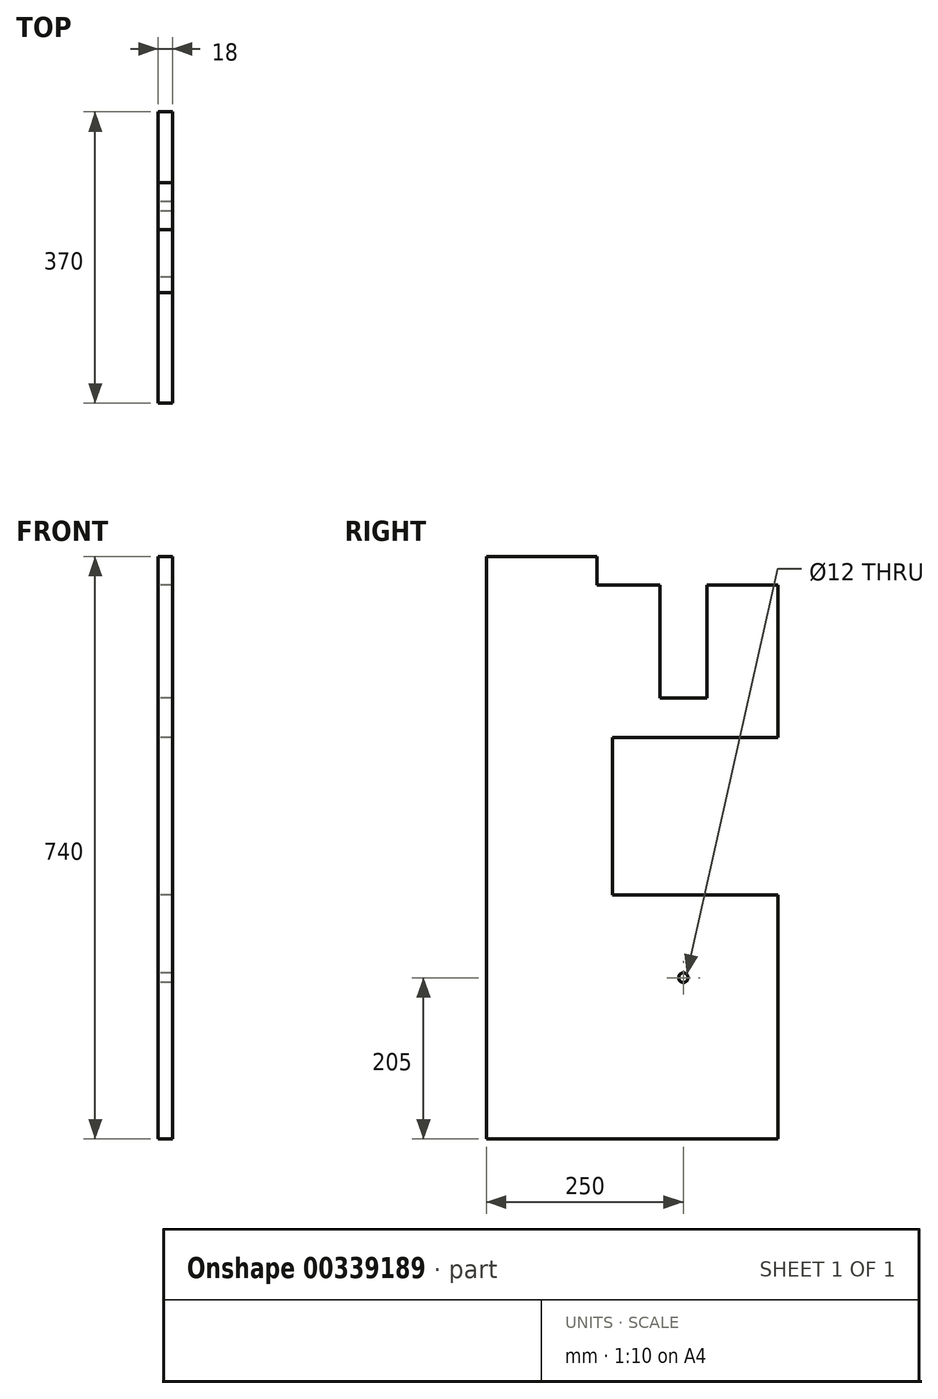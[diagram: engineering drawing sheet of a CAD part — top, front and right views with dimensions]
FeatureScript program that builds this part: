
annotation { "Feature Type Name" : "Feature", "Feature Type Description" : "" }
export const myFeature = defineFeature(function(context is Context, id is Id, definition is map)
    precondition{}
    {
        {
            var Q0;
            Q0=qCreatedBy(makeId("Right.planeOp"),FACE);
            var sketch = newSketch(context, id + "F0", { "sketchPlane" : qUnion([Q0])});
            skLineSegment(sketch, "E0", {"start": v(0, 0) * mm, "end": v(0, 740) * mm});
            skLineSegment(sketch, "E1", {"start": v(0, 740) * mm, "end": v(140, 740) * mm});
            skLineSegment(sketch, "E2", {"start": v(370, 704) * mm, "end": v(370, 510) * mm});
            skLineSegment(sketch, "E3", {"start": v(0, 0) * mm, "end": v(370, 0) * mm});
            skLineSegment(sketch, "E4", {"start": v(370, 0) * mm, "end": v(370, 310) * mm});
            skLineSegment(sketch, "E5", {"start": v(370, 310) * mm, "end": v(160, 310) * mm});
            skLineSegment(sketch, "E6", {"start": v(160, 310) * mm, "end": v(160, 510) * mm});
            skLineSegment(sketch, "E7", {"start": v(160, 510) * mm, "end": v(370, 510) * mm});
            skCircle(sketch, "E8", {"center": v(250, 205) * mm, "radius": 6 * mm});
            skLineSegment(sketch, "E9.top", {"start": v(220, 560) * mm, "end": v(280, 560) * mm});
            skLineSegment(sketch, "E9.left", {"start": v(220, 704) * mm, "end": v(220, 560) * mm});
            skLineSegment(sketch, "E9.right", {"start": v(280, 704) * mm, "end": v(280, 560) * mm});
            skLineSegment(sketch, "E10", {"start": v(370, 704) * mm, "end": v(280, 704) * mm});
            skLineSegment(sketch, "E11", {"start": v(140, 704) * mm, "end": v(140, 740) * mm});
            skLineSegment(sketch, "E12.trimOffspring", {"start": v(220, 704) * mm, "end": v(140, 704) * mm});
            skPoint(sketch, "E13.orphan", {"position": v(370, 740) * mm});
            skSolve(sketch);
        }
        {
            var Q0;
            Q0=makeQuery(id+"F0.imprint","IMPRINT",FACE,{"disambiguationData":[TD([[makeQuery(id+"F0.imprint","IMPRINT",EDGE,{"derivedFrom":sQuery(id+"F0.wireOp",EDGE,"E0")}),-1.0]])]});
            extrude(context, id + "F1", {"entities" : qUnion([Q0]), "depth" : 18 * mm});
        }
    });
